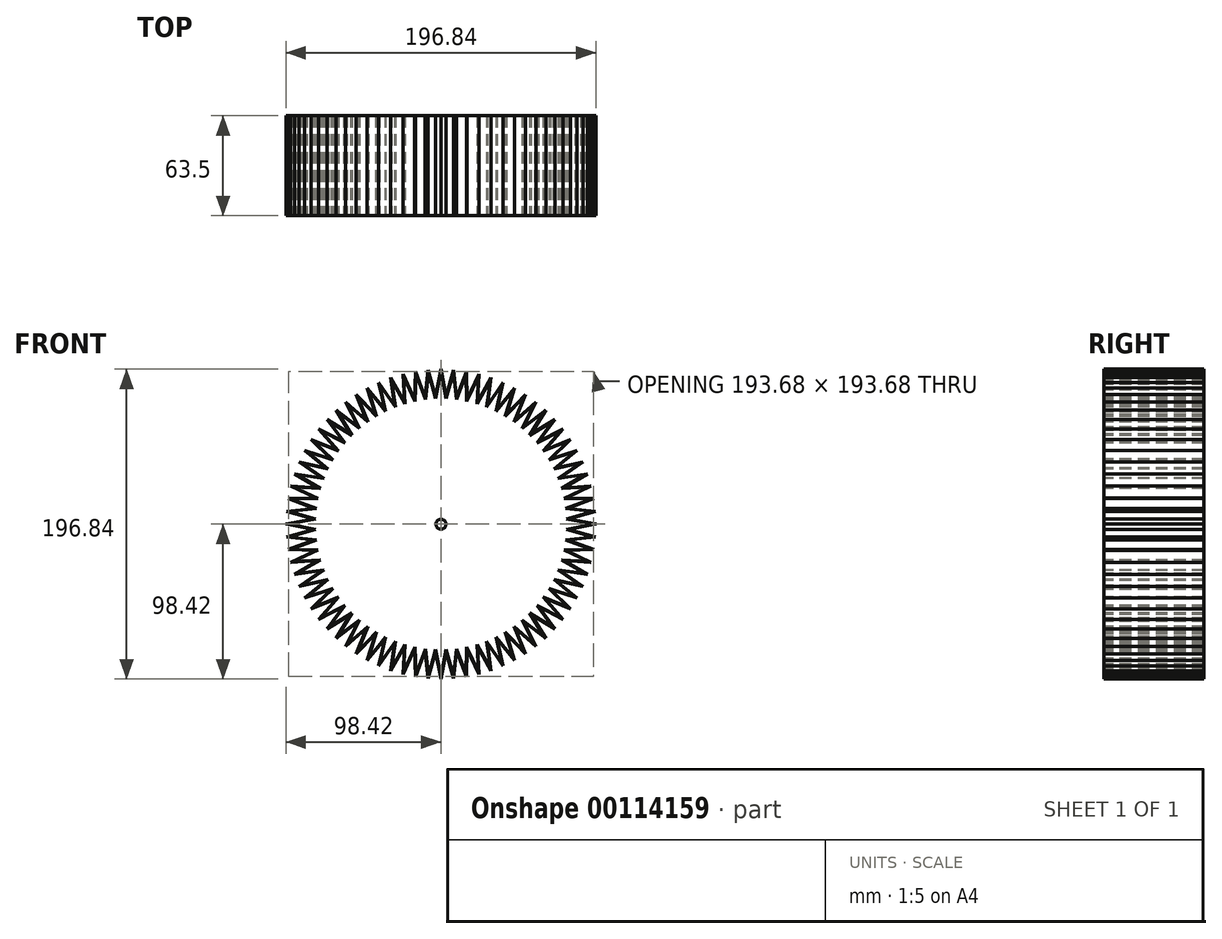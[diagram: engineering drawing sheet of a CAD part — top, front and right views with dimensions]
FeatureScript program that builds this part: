
annotation { "Feature Type Name" : "Feature", "Feature Type Description" : "" }
export const myFeature = defineFeature(function(context is Context, id is Id, definition is map)
    precondition{}
    {
        {
            var Q0;
            Q0=qCreatedBy(makeId("Front.planeOp"),FACE);
            var sketch = newSketch(context, id + "F0", { "sketchPlane" : qUnion([Q0])});
            skCircle(sketch, "E0", {"center": v(0, 0) * mm, "radius": 98.43 * mm});
            skCircle(sketch, "E1", {"center": v(0, 0) * mm, "radius": 79.38 * mm});
            skPoint(sketch, "E2", {"position": v(0, 98.43) * mm});
            skPoint(sketch, "E3", {"position": v(0, 96.84) * mm});
            skPoint(sketch, "E4", {"position": v(-3.37, 80.9) * mm});
            skPoint(sketch, "E5", {"position": v(3.37, 80.9) * mm});
            skLineSegment(sketch, "E6", {"start": v(0, 96.84) * mm, "end": v(-3.37, 79.3) * mm});
            skLineSegment(sketch, "E7", {"start": v(0, 96.84) * mm, "end": v(3.37, 79.3) * mm});
            skLineSegment(sketch, "E8", {"start": v(3.37, 80.9) * mm, "end": v(0, 98.43) * mm});
            skLineSegment(sketch, "E9", {"start": v(0, 98.43) * mm, "end": v(-3.37, 80.9) * mm});
            skLineSegment(sketch, "E10.1.0", {"start": v(-8, 96.5) * mm, "end": v(-9.9, 78.75) * mm});
            skPoint(sketch, "E10.1.1", {"position": v(-8.13, 98.09) * mm});
            skPoint(sketch, "E10.1.2", {"position": v(-8, 96.5) * mm});
            skPoint(sketch, "E10.1.3", {"position": v(-10.04, 80.34) * mm});
            skLineSegment(sketch, "E10.1.4", {"start": v(-8.13, 98.09) * mm, "end": v(-10.04, 80.34) * mm});
            skPoint(sketch, "E10.1.5", {"position": v(-3.32, 80.9) * mm});
            skLineSegment(sketch, "E10.1.6", {"start": v(-8, 96.5) * mm, "end": v(-3.19, 79.31) * mm});
            skLineSegment(sketch, "E10.1.7", {"start": v(-3.32, 80.9) * mm, "end": v(-8.13, 98.09) * mm});
            skLineSegment(sketch, "E10.2.0", {"start": v(-15.94, 95.52) * mm, "end": v(-16.38, 77.67) * mm});
            skPoint(sketch, "E10.2.1", {"position": v(-16.2, 97.08) * mm});
            skPoint(sketch, "E10.2.2", {"position": v(-15.94, 95.52) * mm});
            skPoint(sketch, "E10.2.3", {"position": v(-16.64, 79.23) * mm});
            skLineSegment(sketch, "E10.2.4", {"start": v(-16.2, 97.08) * mm, "end": v(-16.64, 79.23) * mm});
            skPoint(sketch, "E10.2.5", {"position": v(-9.99, 80.34) * mm});
            skLineSegment(sketch, "E10.2.6", {"start": v(-15.94, 95.52) * mm, "end": v(-9.73, 78.78) * mm});
            skLineSegment(sketch, "E10.2.7", {"start": v(-9.99, 80.34) * mm, "end": v(-16.2, 97.08) * mm});
            skLineSegment(sketch, "E10.3.0", {"start": v(-23.77, 93.87) * mm, "end": v(-22.74, 76.05) * mm});
            skPoint(sketch, "E10.3.1", {"position": v(-24.16, 95.41) * mm});
            skPoint(sketch, "E10.3.2", {"position": v(-23.77, 93.87) * mm});
            skPoint(sketch, "E10.3.3", {"position": v(-23.13, 77.59) * mm});
            skLineSegment(sketch, "E10.3.4", {"start": v(-24.16, 95.41) * mm, "end": v(-23.13, 77.59) * mm});
            skPoint(sketch, "E10.3.5", {"position": v(-16.59, 79.24) * mm});
            skLineSegment(sketch, "E10.3.6", {"start": v(-23.77, 93.87) * mm, "end": v(-16.2, 77.7) * mm});
            skLineSegment(sketch, "E10.3.7", {"start": v(-16.59, 79.24) * mm, "end": v(-24.16, 95.41) * mm});
            skLineSegment(sketch, "E10.4.0", {"start": v(-31.44, 91.6) * mm, "end": v(-28.94, 73.91) * mm});
            skPoint(sketch, "E10.4.1", {"position": v(-31.96, 93.1) * mm});
            skPoint(sketch, "E10.4.2", {"position": v(-31.44, 91.6) * mm});
            skPoint(sketch, "E10.4.3", {"position": v(-29.45, 75.41) * mm});
            skLineSegment(sketch, "E10.4.4", {"start": v(-31.96, 93.1) * mm, "end": v(-29.45, 75.41) * mm});
            skPoint(sketch, "E10.4.5", {"position": v(-23.08, 77.6) * mm});
            skLineSegment(sketch, "E10.4.6", {"start": v(-31.44, 91.6) * mm, "end": v(-22.56, 76.1) * mm});
            skLineSegment(sketch, "E10.4.7", {"start": v(-23.08, 77.6) * mm, "end": v(-31.96, 93.1) * mm});
            skLineSegment(sketch, "E10.5.0", {"start": v(-38.9, 88.68) * mm, "end": v(-34.94, 71.27) * mm});
            skPoint(sketch, "E10.5.1", {"position": v(-39.54, 90.13) * mm});
            skPoint(sketch, "E10.5.2", {"position": v(-38.9, 88.68) * mm});
            skPoint(sketch, "E10.5.3", {"position": v(-35.58, 72.72) * mm});
            skLineSegment(sketch, "E10.5.4", {"start": v(-39.54, 90.13) * mm, "end": v(-35.58, 72.72) * mm});
            skPoint(sketch, "E10.5.5", {"position": v(-29.4, 75.43) * mm});
            skLineSegment(sketch, "E10.5.6", {"start": v(-38.9, 88.68) * mm, "end": v(-28.77, 73.98) * mm});
            skLineSegment(sketch, "E10.5.7", {"start": v(-29.4, 75.43) * mm, "end": v(-39.54, 90.13) * mm});
            skLineSegment(sketch, "E10.6.0", {"start": v(-46.09, 85.17) * mm, "end": v(-40.7, 68.14) * mm});
            skPoint(sketch, "E10.6.1", {"position": v(-46.85, 86.56) * mm});
            skPoint(sketch, "E10.6.2", {"position": v(-46.09, 85.17) * mm});
            skPoint(sketch, "E10.6.3", {"position": v(-41.47, 69.54) * mm});
            skLineSegment(sketch, "E10.6.4", {"start": v(-46.85, 86.56) * mm, "end": v(-41.47, 69.54) * mm});
            skPoint(sketch, "E10.6.5", {"position": v(-35.53, 72.75) * mm});
            skLineSegment(sketch, "E10.6.6", {"start": v(-46.09, 85.17) * mm, "end": v(-34.78, 71.35) * mm});
            skLineSegment(sketch, "E10.6.7", {"start": v(-35.53, 72.75) * mm, "end": v(-46.85, 86.56) * mm});
            skLineSegment(sketch, "E10.7.0", {"start": v(-52.97, 81.07) * mm, "end": v(-46.2, 64.55) * mm});
            skPoint(sketch, "E10.7.1", {"position": v(-53.83, 82.4) * mm});
            skPoint(sketch, "E10.7.2", {"position": v(-52.97, 81.07) * mm});
            skPoint(sketch, "E10.7.3", {"position": v(-47.07, 65.87) * mm});
            skLineSegment(sketch, "E10.7.4", {"start": v(-53.83, 82.4) * mm, "end": v(-47.07, 65.87) * mm});
            skPoint(sketch, "E10.7.5", {"position": v(-41.42, 69.56) * mm});
            skLineSegment(sketch, "E10.7.6", {"start": v(-52.97, 81.07) * mm, "end": v(-40.55, 68.23) * mm});
            skLineSegment(sketch, "E10.7.7", {"start": v(-41.42, 69.56) * mm, "end": v(-53.83, 82.4) * mm});
            skLineSegment(sketch, "E10.8.0", {"start": v(-59.48, 76.42) * mm, "end": v(-51.37, 60.51) * mm});
            skPoint(sketch, "E10.8.1", {"position": v(-60.45, 77.67) * mm});
            skPoint(sketch, "E10.8.2", {"position": v(-59.48, 76.42) * mm});
            skPoint(sketch, "E10.8.3", {"position": v(-52.34, 61.76) * mm});
            skLineSegment(sketch, "E10.8.4", {"start": v(-60.45, 77.67) * mm, "end": v(-52.34, 61.76) * mm});
            skPoint(sketch, "E10.8.5", {"position": v(-47.02, 65.9) * mm});
            skLineSegment(sketch, "E10.8.6", {"start": v(-59.48, 76.42) * mm, "end": v(-46.05, 64.65) * mm});
            skLineSegment(sketch, "E10.8.7", {"start": v(-47.02, 65.9) * mm, "end": v(-60.45, 77.67) * mm});
            skLineSegment(sketch, "E10.9.0", {"start": v(-65.59, 71.25) * mm, "end": v(-56.2, 56.06) * mm});
            skPoint(sketch, "E10.9.1", {"position": v(-66.66, 72.41) * mm});
            skPoint(sketch, "E10.9.2", {"position": v(-65.59, 71.25) * mm});
            skPoint(sketch, "E10.9.3", {"position": v(-57.27, 57.23) * mm});
            skLineSegment(sketch, "E10.9.4", {"start": v(-66.66, 72.41) * mm, "end": v(-57.27, 57.23) * mm});
            skPoint(sketch, "E10.9.5", {"position": v(-52.3, 61.8) * mm});
            skLineSegment(sketch, "E10.9.6", {"start": v(-65.59, 71.25) * mm, "end": v(-51.23, 60.63) * mm});
            skLineSegment(sketch, "E10.9.7", {"start": v(-52.3, 61.8) * mm, "end": v(-66.66, 72.41) * mm});
            skLineSegment(sketch, "E10.10.0", {"start": v(-71.25, 65.59) * mm, "end": v(-60.63, 51.23) * mm});
            skPoint(sketch, "E10.10.1", {"position": v(-72.41, 66.66) * mm});
            skPoint(sketch, "E10.10.2", {"position": v(-71.25, 65.59) * mm});
            skPoint(sketch, "E10.10.3", {"position": v(-61.8, 52.3) * mm});
            skLineSegment(sketch, "E10.10.4", {"start": v(-72.41, 66.66) * mm, "end": v(-61.8, 52.3) * mm});
            skPoint(sketch, "E10.10.5", {"position": v(-57.23, 57.27) * mm});
            skLineSegment(sketch, "E10.10.6", {"start": v(-71.25, 65.59) * mm, "end": v(-56.06, 56.2) * mm});
            skLineSegment(sketch, "E10.10.7", {"start": v(-57.23, 57.27) * mm, "end": v(-72.41, 66.66) * mm});
            skLineSegment(sketch, "E10.11.0", {"start": v(-76.42, 59.48) * mm, "end": v(-64.65, 46.05) * mm});
            skPoint(sketch, "E10.11.1", {"position": v(-77.67, 60.45) * mm});
            skPoint(sketch, "E10.11.2", {"position": v(-76.42, 59.48) * mm});
            skPoint(sketch, "E10.11.3", {"position": v(-65.9, 47.02) * mm});
            skLineSegment(sketch, "E10.11.4", {"start": v(-77.67, 60.45) * mm, "end": v(-65.9, 47.02) * mm});
            skPoint(sketch, "E10.11.5", {"position": v(-61.76, 52.34) * mm});
            skLineSegment(sketch, "E10.11.6", {"start": v(-76.42, 59.48) * mm, "end": v(-60.51, 51.37) * mm});
            skLineSegment(sketch, "E10.11.7", {"start": v(-61.76, 52.34) * mm, "end": v(-77.67, 60.45) * mm});
            skLineSegment(sketch, "E10.12.0", {"start": v(-81.07, 52.97) * mm, "end": v(-68.23, 40.55) * mm});
            skPoint(sketch, "E10.12.1", {"position": v(-82.4, 53.83) * mm});
            skPoint(sketch, "E10.12.2", {"position": v(-81.07, 52.97) * mm});
            skPoint(sketch, "E10.12.3", {"position": v(-69.56, 41.42) * mm});
            skLineSegment(sketch, "E10.12.4", {"start": v(-82.4, 53.83) * mm, "end": v(-69.56, 41.42) * mm});
            skPoint(sketch, "E10.12.5", {"position": v(-65.87, 47.07) * mm});
            skLineSegment(sketch, "E10.12.6", {"start": v(-81.07, 52.97) * mm, "end": v(-64.55, 46.2) * mm});
            skLineSegment(sketch, "E10.12.7", {"start": v(-65.87, 47.07) * mm, "end": v(-82.4, 53.83) * mm});
            skLineSegment(sketch, "E10.13.0", {"start": v(-85.17, 46.09) * mm, "end": v(-71.35, 34.78) * mm});
            skPoint(sketch, "E10.13.1", {"position": v(-86.56, 46.85) * mm});
            skPoint(sketch, "E10.13.2", {"position": v(-85.17, 46.09) * mm});
            skPoint(sketch, "E10.13.3", {"position": v(-72.75, 35.53) * mm});
            skLineSegment(sketch, "E10.13.4", {"start": v(-86.56, 46.85) * mm, "end": v(-72.75, 35.53) * mm});
            skPoint(sketch, "E10.13.5", {"position": v(-69.54, 41.47) * mm});
            skLineSegment(sketch, "E10.13.6", {"start": v(-85.17, 46.09) * mm, "end": v(-68.14, 40.7) * mm});
            skLineSegment(sketch, "E10.13.7", {"start": v(-69.54, 41.47) * mm, "end": v(-86.56, 46.85) * mm});
            skLineSegment(sketch, "E10.14.0", {"start": v(-88.68, 38.9) * mm, "end": v(-73.98, 28.77) * mm});
            skPoint(sketch, "E10.14.1", {"position": v(-90.13, 39.54) * mm});
            skPoint(sketch, "E10.14.2", {"position": v(-88.68, 38.9) * mm});
            skPoint(sketch, "E10.14.3", {"position": v(-75.43, 29.4) * mm});
            skLineSegment(sketch, "E10.14.4", {"start": v(-90.13, 39.54) * mm, "end": v(-75.43, 29.4) * mm});
            skPoint(sketch, "E10.14.5", {"position": v(-72.72, 35.58) * mm});
            skLineSegment(sketch, "E10.14.6", {"start": v(-88.68, 38.9) * mm, "end": v(-71.27, 34.94) * mm});
            skLineSegment(sketch, "E10.14.7", {"start": v(-72.72, 35.58) * mm, "end": v(-90.13, 39.54) * mm});
            skLineSegment(sketch, "E10.15.0", {"start": v(-91.6, 31.44) * mm, "end": v(-76.1, 22.56) * mm});
            skPoint(sketch, "E10.15.1", {"position": v(-93.1, 31.96) * mm});
            skPoint(sketch, "E10.15.2", {"position": v(-91.6, 31.44) * mm});
            skPoint(sketch, "E10.15.3", {"position": v(-77.6, 23.08) * mm});
            skLineSegment(sketch, "E10.15.4", {"start": v(-93.1, 31.96) * mm, "end": v(-77.6, 23.08) * mm});
            skPoint(sketch, "E10.15.5", {"position": v(-75.41, 29.45) * mm});
            skLineSegment(sketch, "E10.15.6", {"start": v(-91.6, 31.44) * mm, "end": v(-73.91, 28.94) * mm});
            skLineSegment(sketch, "E10.15.7", {"start": v(-75.41, 29.45) * mm, "end": v(-93.1, 31.96) * mm});
            skLineSegment(sketch, "E10.16.0", {"start": v(-93.87, 23.77) * mm, "end": v(-77.7, 16.2) * mm});
            skPoint(sketch, "E10.16.1", {"position": v(-95.41, 24.16) * mm});
            skPoint(sketch, "E10.16.2", {"position": v(-93.87, 23.77) * mm});
            skPoint(sketch, "E10.16.3", {"position": v(-79.24, 16.59) * mm});
            skLineSegment(sketch, "E10.16.4", {"start": v(-95.41, 24.16) * mm, "end": v(-79.24, 16.59) * mm});
            skPoint(sketch, "E10.16.5", {"position": v(-77.59, 23.13) * mm});
            skLineSegment(sketch, "E10.16.6", {"start": v(-93.87, 23.77) * mm, "end": v(-76.05, 22.74) * mm});
            skLineSegment(sketch, "E10.16.7", {"start": v(-77.59, 23.13) * mm, "end": v(-95.41, 24.16) * mm});
            skLineSegment(sketch, "E10.17.0", {"start": v(-95.52, 15.94) * mm, "end": v(-78.78, 9.73) * mm});
            skPoint(sketch, "E10.17.1", {"position": v(-97.08, 16.2) * mm});
            skPoint(sketch, "E10.17.2", {"position": v(-95.52, 15.94) * mm});
            skPoint(sketch, "E10.17.3", {"position": v(-80.34, 9.99) * mm});
            skLineSegment(sketch, "E10.17.4", {"start": v(-97.08, 16.2) * mm, "end": v(-80.34, 9.99) * mm});
            skPoint(sketch, "E10.17.5", {"position": v(-79.23, 16.64) * mm});
            skLineSegment(sketch, "E10.17.6", {"start": v(-95.52, 15.94) * mm, "end": v(-77.67, 16.38) * mm});
            skLineSegment(sketch, "E10.17.7", {"start": v(-79.23, 16.64) * mm, "end": v(-97.08, 16.2) * mm});
            skLineSegment(sketch, "E10.18.0", {"start": v(-96.5, 8) * mm, "end": v(-79.31, 3.19) * mm});
            skPoint(sketch, "E10.18.1", {"position": v(-98.09, 8.13) * mm});
            skPoint(sketch, "E10.18.2", {"position": v(-96.5, 8) * mm});
            skPoint(sketch, "E10.18.3", {"position": v(-80.9, 3.32) * mm});
            skLineSegment(sketch, "E10.18.4", {"start": v(-98.09, 8.13) * mm, "end": v(-80.9, 3.32) * mm});
            skPoint(sketch, "E10.18.5", {"position": v(-80.34, 10.04) * mm});
            skLineSegment(sketch, "E10.18.6", {"start": v(-96.5, 8) * mm, "end": v(-78.75, 9.9) * mm});
            skLineSegment(sketch, "E10.18.7", {"start": v(-80.34, 10.04) * mm, "end": v(-98.09, 8.13) * mm});
            skLineSegment(sketch, "E10.19.0", {"start": v(-96.84, 0) * mm, "end": v(-79.3, -3.37) * mm});
            skPoint(sketch, "E10.19.1", {"position": v(-98.43, 0) * mm});
            skPoint(sketch, "E10.19.2", {"position": v(-96.84, 0) * mm});
            skPoint(sketch, "E10.19.3", {"position": v(-80.9, -3.37) * mm});
            skLineSegment(sketch, "E10.19.4", {"start": v(-98.43, 0) * mm, "end": v(-80.9, -3.37) * mm});
            skPoint(sketch, "E10.19.5", {"position": v(-80.9, 3.37) * mm});
            skLineSegment(sketch, "E10.19.6", {"start": v(-96.84, 0) * mm, "end": v(-79.3, 3.37) * mm});
            skLineSegment(sketch, "E10.19.7", {"start": v(-80.9, 3.37) * mm, "end": v(-98.42, 0) * mm});
            skLineSegment(sketch, "E10.20.0", {"start": v(-96.5, -8) * mm, "end": v(-78.75, -9.9) * mm});
            skPoint(sketch, "E10.20.1", {"position": v(-98.09, -8.13) * mm});
            skPoint(sketch, "E10.20.2", {"position": v(-96.5, -8) * mm});
            skPoint(sketch, "E10.20.3", {"position": v(-80.34, -10.04) * mm});
            skLineSegment(sketch, "E10.20.4", {"start": v(-98.09, -8.13) * mm, "end": v(-80.34, -10.04) * mm});
            skPoint(sketch, "E10.20.5", {"position": v(-80.9, -3.32) * mm});
            skLineSegment(sketch, "E10.20.6", {"start": v(-96.5, -8) * mm, "end": v(-79.31, -3.19) * mm});
            skLineSegment(sketch, "E10.20.7", {"start": v(-80.9, -3.32) * mm, "end": v(-98.09, -8.13) * mm});
            skLineSegment(sketch, "E10.21.0", {"start": v(-95.52, -15.94) * mm, "end": v(-77.67, -16.38) * mm});
            skPoint(sketch, "E10.21.1", {"position": v(-97.08, -16.2) * mm});
            skPoint(sketch, "E10.21.2", {"position": v(-95.52, -15.94) * mm});
            skPoint(sketch, "E10.21.3", {"position": v(-79.23, -16.64) * mm});
            skLineSegment(sketch, "E10.21.4", {"start": v(-97.08, -16.2) * mm, "end": v(-79.23, -16.64) * mm});
            skPoint(sketch, "E10.21.5", {"position": v(-80.34, -9.99) * mm});
            skLineSegment(sketch, "E10.21.6", {"start": v(-95.52, -15.94) * mm, "end": v(-78.78, -9.73) * mm});
            skLineSegment(sketch, "E10.21.7", {"start": v(-80.34, -9.99) * mm, "end": v(-97.08, -16.2) * mm});
            skLineSegment(sketch, "E10.22.0", {"start": v(-93.87, -23.77) * mm, "end": v(-76.05, -22.74) * mm});
            skPoint(sketch, "E10.22.1", {"position": v(-95.41, -24.16) * mm});
            skPoint(sketch, "E10.22.2", {"position": v(-93.87, -23.77) * mm});
            skPoint(sketch, "E10.22.3", {"position": v(-77.59, -23.13) * mm});
            skLineSegment(sketch, "E10.22.4", {"start": v(-95.41, -24.16) * mm, "end": v(-77.59, -23.13) * mm});
            skPoint(sketch, "E10.22.5", {"position": v(-79.24, -16.59) * mm});
            skLineSegment(sketch, "E10.22.6", {"start": v(-93.87, -23.77) * mm, "end": v(-77.7, -16.2) * mm});
            skLineSegment(sketch, "E10.22.7", {"start": v(-79.24, -16.59) * mm, "end": v(-95.41, -24.16) * mm});
            skLineSegment(sketch, "E10.23.0", {"start": v(-91.6, -31.44) * mm, "end": v(-73.91, -28.94) * mm});
            skPoint(sketch, "E10.23.1", {"position": v(-93.1, -31.96) * mm});
            skPoint(sketch, "E10.23.2", {"position": v(-91.6, -31.44) * mm});
            skPoint(sketch, "E10.23.3", {"position": v(-75.41, -29.45) * mm});
            skLineSegment(sketch, "E10.23.4", {"start": v(-93.1, -31.96) * mm, "end": v(-75.41, -29.45) * mm});
            skPoint(sketch, "E10.23.5", {"position": v(-77.6, -23.08) * mm});
            skLineSegment(sketch, "E10.23.6", {"start": v(-91.6, -31.44) * mm, "end": v(-76.1, -22.56) * mm});
            skLineSegment(sketch, "E10.23.7", {"start": v(-77.6, -23.08) * mm, "end": v(-93.1, -31.96) * mm});
            skLineSegment(sketch, "E10.24.0", {"start": v(-88.68, -38.9) * mm, "end": v(-71.27, -34.94) * mm});
            skPoint(sketch, "E10.24.1", {"position": v(-90.13, -39.54) * mm});
            skPoint(sketch, "E10.24.2", {"position": v(-88.68, -38.9) * mm});
            skPoint(sketch, "E10.24.3", {"position": v(-72.72, -35.58) * mm});
            skLineSegment(sketch, "E10.24.4", {"start": v(-90.13, -39.54) * mm, "end": v(-72.72, -35.58) * mm});
            skPoint(sketch, "E10.24.5", {"position": v(-75.43, -29.4) * mm});
            skLineSegment(sketch, "E10.24.6", {"start": v(-88.68, -38.9) * mm, "end": v(-73.98, -28.77) * mm});
            skLineSegment(sketch, "E10.24.7", {"start": v(-75.43, -29.4) * mm, "end": v(-90.13, -39.54) * mm});
            skLineSegment(sketch, "E10.25.0", {"start": v(-85.17, -46.09) * mm, "end": v(-68.14, -40.7) * mm});
            skPoint(sketch, "E10.25.1", {"position": v(-86.56, -46.85) * mm});
            skPoint(sketch, "E10.25.2", {"position": v(-85.17, -46.09) * mm});
            skPoint(sketch, "E10.25.3", {"position": v(-69.54, -41.47) * mm});
            skLineSegment(sketch, "E10.25.4", {"start": v(-86.56, -46.85) * mm, "end": v(-69.54, -41.47) * mm});
            skPoint(sketch, "E10.25.5", {"position": v(-72.75, -35.53) * mm});
            skLineSegment(sketch, "E10.25.6", {"start": v(-85.17, -46.09) * mm, "end": v(-71.35, -34.78) * mm});
            skLineSegment(sketch, "E10.25.7", {"start": v(-72.75, -35.53) * mm, "end": v(-86.56, -46.85) * mm});
            skLineSegment(sketch, "E10.26.0", {"start": v(-81.07, -52.97) * mm, "end": v(-64.55, -46.2) * mm});
            skPoint(sketch, "E10.26.1", {"position": v(-82.4, -53.83) * mm});
            skPoint(sketch, "E10.26.2", {"position": v(-81.07, -52.97) * mm});
            skPoint(sketch, "E10.26.3", {"position": v(-65.87, -47.07) * mm});
            skLineSegment(sketch, "E10.26.4", {"start": v(-82.4, -53.83) * mm, "end": v(-65.87, -47.07) * mm});
            skPoint(sketch, "E10.26.5", {"position": v(-69.56, -41.42) * mm});
            skLineSegment(sketch, "E10.26.6", {"start": v(-81.07, -52.97) * mm, "end": v(-68.23, -40.55) * mm});
            skLineSegment(sketch, "E10.26.7", {"start": v(-69.56, -41.42) * mm, "end": v(-82.4, -53.83) * mm});
            skLineSegment(sketch, "E10.27.0", {"start": v(-76.42, -59.48) * mm, "end": v(-60.51, -51.37) * mm});
            skPoint(sketch, "E10.27.1", {"position": v(-77.67, -60.45) * mm});
            skPoint(sketch, "E10.27.2", {"position": v(-76.42, -59.48) * mm});
            skPoint(sketch, "E10.27.3", {"position": v(-61.76, -52.34) * mm});
            skLineSegment(sketch, "E10.27.4", {"start": v(-77.67, -60.45) * mm, "end": v(-61.76, -52.34) * mm});
            skPoint(sketch, "E10.27.5", {"position": v(-65.9, -47.02) * mm});
            skLineSegment(sketch, "E10.27.6", {"start": v(-76.42, -59.48) * mm, "end": v(-64.65, -46.05) * mm});
            skLineSegment(sketch, "E10.27.7", {"start": v(-65.9, -47.02) * mm, "end": v(-77.67, -60.45) * mm});
            skLineSegment(sketch, "E10.28.0", {"start": v(-71.25, -65.59) * mm, "end": v(-56.06, -56.2) * mm});
            skPoint(sketch, "E10.28.1", {"position": v(-72.41, -66.66) * mm});
            skPoint(sketch, "E10.28.2", {"position": v(-71.25, -65.59) * mm});
            skPoint(sketch, "E10.28.3", {"position": v(-57.23, -57.27) * mm});
            skLineSegment(sketch, "E10.28.4", {"start": v(-72.41, -66.66) * mm, "end": v(-57.23, -57.27) * mm});
            skPoint(sketch, "E10.28.5", {"position": v(-61.8, -52.3) * mm});
            skLineSegment(sketch, "E10.28.6", {"start": v(-71.25, -65.59) * mm, "end": v(-60.63, -51.23) * mm});
            skLineSegment(sketch, "E10.28.7", {"start": v(-61.8, -52.3) * mm, "end": v(-72.41, -66.66) * mm});
            skLineSegment(sketch, "E10.29.0", {"start": v(-65.59, -71.25) * mm, "end": v(-51.23, -60.63) * mm});
            skPoint(sketch, "E10.29.1", {"position": v(-66.66, -72.41) * mm});
            skPoint(sketch, "E10.29.2", {"position": v(-65.59, -71.25) * mm});
            skPoint(sketch, "E10.29.3", {"position": v(-52.3, -61.8) * mm});
            skLineSegment(sketch, "E10.29.4", {"start": v(-66.66, -72.41) * mm, "end": v(-52.3, -61.8) * mm});
            skPoint(sketch, "E10.29.5", {"position": v(-57.27, -57.23) * mm});
            skLineSegment(sketch, "E10.29.6", {"start": v(-65.59, -71.25) * mm, "end": v(-56.2, -56.06) * mm});
            skLineSegment(sketch, "E10.29.7", {"start": v(-57.27, -57.23) * mm, "end": v(-66.66, -72.41) * mm});
            skLineSegment(sketch, "E10.30.0", {"start": v(-59.48, -76.42) * mm, "end": v(-46.05, -64.65) * mm});
            skPoint(sketch, "E10.30.1", {"position": v(-60.45, -77.67) * mm});
            skPoint(sketch, "E10.30.2", {"position": v(-59.48, -76.42) * mm});
            skPoint(sketch, "E10.30.3", {"position": v(-47.02, -65.9) * mm});
            skLineSegment(sketch, "E10.30.4", {"start": v(-60.45, -77.67) * mm, "end": v(-47.02, -65.9) * mm});
            skPoint(sketch, "E10.30.5", {"position": v(-52.34, -61.76) * mm});
            skLineSegment(sketch, "E10.30.6", {"start": v(-59.48, -76.42) * mm, "end": v(-51.37, -60.51) * mm});
            skLineSegment(sketch, "E10.30.7", {"start": v(-52.34, -61.76) * mm, "end": v(-60.45, -77.67) * mm});
            skLineSegment(sketch, "E10.31.0", {"start": v(-52.97, -81.07) * mm, "end": v(-40.55, -68.23) * mm});
            skPoint(sketch, "E10.31.1", {"position": v(-53.83, -82.4) * mm});
            skPoint(sketch, "E10.31.2", {"position": v(-52.97, -81.07) * mm});
            skPoint(sketch, "E10.31.3", {"position": v(-41.42, -69.56) * mm});
            skLineSegment(sketch, "E10.31.4", {"start": v(-53.83, -82.4) * mm, "end": v(-41.42, -69.56) * mm});
            skPoint(sketch, "E10.31.5", {"position": v(-47.07, -65.87) * mm});
            skLineSegment(sketch, "E10.31.6", {"start": v(-52.97, -81.07) * mm, "end": v(-46.2, -64.55) * mm});
            skLineSegment(sketch, "E10.31.7", {"start": v(-47.07, -65.87) * mm, "end": v(-53.83, -82.4) * mm});
            skLineSegment(sketch, "E10.32.0", {"start": v(-46.09, -85.17) * mm, "end": v(-34.78, -71.35) * mm});
            skPoint(sketch, "E10.32.1", {"position": v(-46.85, -86.56) * mm});
            skPoint(sketch, "E10.32.2", {"position": v(-46.09, -85.17) * mm});
            skPoint(sketch, "E10.32.3", {"position": v(-35.53, -72.75) * mm});
            skLineSegment(sketch, "E10.32.4", {"start": v(-46.85, -86.56) * mm, "end": v(-35.53, -72.75) * mm});
            skPoint(sketch, "E10.32.5", {"position": v(-41.47, -69.54) * mm});
            skLineSegment(sketch, "E10.32.6", {"start": v(-46.09, -85.17) * mm, "end": v(-40.7, -68.14) * mm});
            skLineSegment(sketch, "E10.32.7", {"start": v(-41.47, -69.54) * mm, "end": v(-46.85, -86.56) * mm});
            skLineSegment(sketch, "E10.33.0", {"start": v(-38.9, -88.68) * mm, "end": v(-28.77, -73.98) * mm});
            skPoint(sketch, "E10.33.1", {"position": v(-39.54, -90.13) * mm});
            skPoint(sketch, "E10.33.2", {"position": v(-38.9, -88.68) * mm});
            skPoint(sketch, "E10.33.3", {"position": v(-29.4, -75.43) * mm});
            skLineSegment(sketch, "E10.33.4", {"start": v(-39.54, -90.13) * mm, "end": v(-29.4, -75.43) * mm});
            skPoint(sketch, "E10.33.5", {"position": v(-35.58, -72.72) * mm});
            skLineSegment(sketch, "E10.33.6", {"start": v(-38.9, -88.68) * mm, "end": v(-34.94, -71.27) * mm});
            skLineSegment(sketch, "E10.33.7", {"start": v(-35.58, -72.72) * mm, "end": v(-39.54, -90.13) * mm});
            skLineSegment(sketch, "E10.34.0", {"start": v(-31.44, -91.6) * mm, "end": v(-22.56, -76.1) * mm});
            skPoint(sketch, "E10.34.1", {"position": v(-31.96, -93.1) * mm});
            skPoint(sketch, "E10.34.2", {"position": v(-31.44, -91.6) * mm});
            skPoint(sketch, "E10.34.3", {"position": v(-23.08, -77.6) * mm});
            skLineSegment(sketch, "E10.34.4", {"start": v(-31.96, -93.1) * mm, "end": v(-23.08, -77.6) * mm});
            skPoint(sketch, "E10.34.5", {"position": v(-29.45, -75.41) * mm});
            skLineSegment(sketch, "E10.34.6", {"start": v(-31.44, -91.6) * mm, "end": v(-28.94, -73.91) * mm});
            skLineSegment(sketch, "E10.34.7", {"start": v(-29.45, -75.41) * mm, "end": v(-31.96, -93.1) * mm});
            skLineSegment(sketch, "E10.35.0", {"start": v(-23.77, -93.87) * mm, "end": v(-16.2, -77.7) * mm});
            skPoint(sketch, "E10.35.1", {"position": v(-24.16, -95.41) * mm});
            skPoint(sketch, "E10.35.2", {"position": v(-23.77, -93.87) * mm});
            skPoint(sketch, "E10.35.3", {"position": v(-16.59, -79.24) * mm});
            skLineSegment(sketch, "E10.35.4", {"start": v(-24.16, -95.41) * mm, "end": v(-16.59, -79.24) * mm});
            skPoint(sketch, "E10.35.5", {"position": v(-23.13, -77.59) * mm});
            skLineSegment(sketch, "E10.35.6", {"start": v(-23.77, -93.87) * mm, "end": v(-22.74, -76.05) * mm});
            skLineSegment(sketch, "E10.35.7", {"start": v(-23.13, -77.59) * mm, "end": v(-24.16, -95.41) * mm});
            skLineSegment(sketch, "E10.36.0", {"start": v(-15.94, -95.52) * mm, "end": v(-9.73, -78.78) * mm});
            skPoint(sketch, "E10.36.1", {"position": v(-16.2, -97.08) * mm});
            skPoint(sketch, "E10.36.2", {"position": v(-15.94, -95.52) * mm});
            skPoint(sketch, "E10.36.3", {"position": v(-9.99, -80.34) * mm});
            skLineSegment(sketch, "E10.36.4", {"start": v(-16.2, -97.08) * mm, "end": v(-9.99, -80.34) * mm});
            skPoint(sketch, "E10.36.5", {"position": v(-16.64, -79.23) * mm});
            skLineSegment(sketch, "E10.36.6", {"start": v(-15.94, -95.52) * mm, "end": v(-16.38, -77.67) * mm});
            skLineSegment(sketch, "E10.36.7", {"start": v(-16.64, -79.23) * mm, "end": v(-16.2, -97.08) * mm});
            skLineSegment(sketch, "E10.37.0", {"start": v(-8, -96.5) * mm, "end": v(-3.19, -79.31) * mm});
            skPoint(sketch, "E10.37.1", {"position": v(-8.13, -98.09) * mm});
            skPoint(sketch, "E10.37.2", {"position": v(-8, -96.5) * mm});
            skPoint(sketch, "E10.37.3", {"position": v(-3.32, -80.9) * mm});
            skLineSegment(sketch, "E10.37.4", {"start": v(-8.13, -98.09) * mm, "end": v(-3.32, -80.9) * mm});
            skPoint(sketch, "E10.37.5", {"position": v(-10.04, -80.34) * mm});
            skLineSegment(sketch, "E10.37.6", {"start": v(-8, -96.5) * mm, "end": v(-9.9, -78.75) * mm});
            skLineSegment(sketch, "E10.37.7", {"start": v(-10.04, -80.34) * mm, "end": v(-8.13, -98.09) * mm});
            skLineSegment(sketch, "E10.38.0", {"start": v(0, -96.84) * mm, "end": v(3.37, -79.3) * mm});
            skPoint(sketch, "E10.38.1", {"position": v(0, -98.43) * mm});
            skPoint(sketch, "E10.38.2", {"position": v(0, -96.84) * mm});
            skPoint(sketch, "E10.38.3", {"position": v(3.37, -80.9) * mm});
            skLineSegment(sketch, "E10.38.4", {"start": v(0, -98.43) * mm, "end": v(3.37, -80.9) * mm});
            skPoint(sketch, "E10.38.5", {"position": v(-3.37, -80.9) * mm});
            skLineSegment(sketch, "E10.38.6", {"start": v(0, -96.84) * mm, "end": v(-3.37, -79.3) * mm});
            skLineSegment(sketch, "E10.38.7", {"start": v(-3.37, -80.9) * mm, "end": v(0, -98.43) * mm});
            skLineSegment(sketch, "E10.39.0", {"start": v(8, -96.5) * mm, "end": v(9.9, -78.75) * mm});
            skPoint(sketch, "E10.39.1", {"position": v(8.13, -98.09) * mm});
            skPoint(sketch, "E10.39.2", {"position": v(8, -96.5) * mm});
            skPoint(sketch, "E10.39.3", {"position": v(10.04, -80.34) * mm});
            skLineSegment(sketch, "E10.39.4", {"start": v(8.13, -98.09) * mm, "end": v(10.04, -80.34) * mm});
            skPoint(sketch, "E10.39.5", {"position": v(3.32, -80.9) * mm});
            skLineSegment(sketch, "E10.39.6", {"start": v(8, -96.5) * mm, "end": v(3.19, -79.31) * mm});
            skLineSegment(sketch, "E10.39.7", {"start": v(3.32, -80.9) * mm, "end": v(8.13, -98.09) * mm});
            skLineSegment(sketch, "E10.40.0", {"start": v(15.94, -95.52) * mm, "end": v(16.38, -77.67) * mm});
            skPoint(sketch, "E10.40.1", {"position": v(16.2, -97.08) * mm});
            skPoint(sketch, "E10.40.2", {"position": v(15.94, -95.52) * mm});
            skPoint(sketch, "E10.40.3", {"position": v(16.64, -79.23) * mm});
            skLineSegment(sketch, "E10.40.4", {"start": v(16.2, -97.08) * mm, "end": v(16.64, -79.23) * mm});
            skPoint(sketch, "E10.40.5", {"position": v(9.99, -80.34) * mm});
            skLineSegment(sketch, "E10.40.6", {"start": v(15.94, -95.52) * mm, "end": v(9.73, -78.78) * mm});
            skLineSegment(sketch, "E10.40.7", {"start": v(9.99, -80.34) * mm, "end": v(16.2, -97.08) * mm});
            skLineSegment(sketch, "E10.41.0", {"start": v(23.77, -93.87) * mm, "end": v(22.74, -76.05) * mm});
            skPoint(sketch, "E10.41.1", {"position": v(24.16, -95.41) * mm});
            skPoint(sketch, "E10.41.2", {"position": v(23.77, -93.87) * mm});
            skPoint(sketch, "E10.41.3", {"position": v(23.13, -77.59) * mm});
            skLineSegment(sketch, "E10.41.4", {"start": v(24.16, -95.41) * mm, "end": v(23.13, -77.59) * mm});
            skPoint(sketch, "E10.41.5", {"position": v(16.59, -79.24) * mm});
            skLineSegment(sketch, "E10.41.6", {"start": v(23.77, -93.87) * mm, "end": v(16.2, -77.7) * mm});
            skLineSegment(sketch, "E10.41.7", {"start": v(16.59, -79.24) * mm, "end": v(24.16, -95.41) * mm});
            skLineSegment(sketch, "E10.42.0", {"start": v(31.44, -91.6) * mm, "end": v(28.94, -73.91) * mm});
            skPoint(sketch, "E10.42.1", {"position": v(31.96, -93.1) * mm});
            skPoint(sketch, "E10.42.2", {"position": v(31.44, -91.6) * mm});
            skPoint(sketch, "E10.42.3", {"position": v(29.45, -75.41) * mm});
            skLineSegment(sketch, "E10.42.4", {"start": v(31.96, -93.1) * mm, "end": v(29.45, -75.41) * mm});
            skPoint(sketch, "E10.42.5", {"position": v(23.08, -77.6) * mm});
            skLineSegment(sketch, "E10.42.6", {"start": v(31.44, -91.6) * mm, "end": v(22.56, -76.1) * mm});
            skLineSegment(sketch, "E10.42.7", {"start": v(23.08, -77.6) * mm, "end": v(31.96, -93.1) * mm});
            skLineSegment(sketch, "E10.43.0", {"start": v(38.9, -88.68) * mm, "end": v(34.94, -71.27) * mm});
            skPoint(sketch, "E10.43.1", {"position": v(39.54, -90.13) * mm});
            skPoint(sketch, "E10.43.2", {"position": v(38.9, -88.68) * mm});
            skPoint(sketch, "E10.43.3", {"position": v(35.58, -72.72) * mm});
            skLineSegment(sketch, "E10.43.4", {"start": v(39.54, -90.13) * mm, "end": v(35.58, -72.72) * mm});
            skPoint(sketch, "E10.43.5", {"position": v(29.4, -75.43) * mm});
            skLineSegment(sketch, "E10.43.6", {"start": v(38.9, -88.68) * mm, "end": v(28.77, -73.98) * mm});
            skLineSegment(sketch, "E10.43.7", {"start": v(29.4, -75.43) * mm, "end": v(39.54, -90.13) * mm});
            skLineSegment(sketch, "E10.44.0", {"start": v(46.09, -85.17) * mm, "end": v(40.7, -68.14) * mm});
            skPoint(sketch, "E10.44.1", {"position": v(46.85, -86.56) * mm});
            skPoint(sketch, "E10.44.2", {"position": v(46.09, -85.17) * mm});
            skPoint(sketch, "E10.44.3", {"position": v(41.47, -69.54) * mm});
            skLineSegment(sketch, "E10.44.4", {"start": v(46.85, -86.56) * mm, "end": v(41.47, -69.54) * mm});
            skPoint(sketch, "E10.44.5", {"position": v(35.53, -72.75) * mm});
            skLineSegment(sketch, "E10.44.6", {"start": v(46.09, -85.17) * mm, "end": v(34.78, -71.35) * mm});
            skLineSegment(sketch, "E10.44.7", {"start": v(35.53, -72.75) * mm, "end": v(46.85, -86.56) * mm});
            skLineSegment(sketch, "E10.45.0", {"start": v(52.97, -81.07) * mm, "end": v(46.2, -64.55) * mm});
            skPoint(sketch, "E10.45.1", {"position": v(53.83, -82.4) * mm});
            skPoint(sketch, "E10.45.2", {"position": v(52.97, -81.07) * mm});
            skPoint(sketch, "E10.45.3", {"position": v(47.07, -65.87) * mm});
            skLineSegment(sketch, "E10.45.4", {"start": v(53.83, -82.4) * mm, "end": v(47.07, -65.87) * mm});
            skPoint(sketch, "E10.45.5", {"position": v(41.42, -69.56) * mm});
            skLineSegment(sketch, "E10.45.6", {"start": v(52.97, -81.07) * mm, "end": v(40.55, -68.23) * mm});
            skLineSegment(sketch, "E10.45.7", {"start": v(41.42, -69.56) * mm, "end": v(53.83, -82.4) * mm});
            skLineSegment(sketch, "E10.46.0", {"start": v(59.48, -76.42) * mm, "end": v(51.37, -60.51) * mm});
            skPoint(sketch, "E10.46.1", {"position": v(60.45, -77.67) * mm});
            skPoint(sketch, "E10.46.2", {"position": v(59.48, -76.42) * mm});
            skPoint(sketch, "E10.46.3", {"position": v(52.34, -61.76) * mm});
            skLineSegment(sketch, "E10.46.4", {"start": v(60.45, -77.67) * mm, "end": v(52.34, -61.76) * mm});
            skPoint(sketch, "E10.46.5", {"position": v(47.02, -65.9) * mm});
            skLineSegment(sketch, "E10.46.6", {"start": v(59.48, -76.42) * mm, "end": v(46.05, -64.65) * mm});
            skLineSegment(sketch, "E10.46.7", {"start": v(47.02, -65.9) * mm, "end": v(60.45, -77.67) * mm});
            skLineSegment(sketch, "E10.47.0", {"start": v(65.59, -71.25) * mm, "end": v(56.2, -56.06) * mm});
            skPoint(sketch, "E10.47.1", {"position": v(66.66, -72.41) * mm});
            skPoint(sketch, "E10.47.2", {"position": v(65.59, -71.25) * mm});
            skPoint(sketch, "E10.47.3", {"position": v(57.27, -57.23) * mm});
            skLineSegment(sketch, "E10.47.4", {"start": v(66.66, -72.41) * mm, "end": v(57.27, -57.23) * mm});
            skPoint(sketch, "E10.47.5", {"position": v(52.3, -61.8) * mm});
            skLineSegment(sketch, "E10.47.6", {"start": v(65.59, -71.25) * mm, "end": v(51.23, -60.63) * mm});
            skLineSegment(sketch, "E10.47.7", {"start": v(52.3, -61.8) * mm, "end": v(66.66, -72.41) * mm});
            skLineSegment(sketch, "E10.48.0", {"start": v(71.25, -65.59) * mm, "end": v(60.63, -51.23) * mm});
            skPoint(sketch, "E10.48.1", {"position": v(72.41, -66.66) * mm});
            skPoint(sketch, "E10.48.2", {"position": v(71.25, -65.59) * mm});
            skPoint(sketch, "E10.48.3", {"position": v(61.8, -52.3) * mm});
            skLineSegment(sketch, "E10.48.4", {"start": v(72.41, -66.66) * mm, "end": v(61.8, -52.3) * mm});
            skPoint(sketch, "E10.48.5", {"position": v(57.23, -57.27) * mm});
            skLineSegment(sketch, "E10.48.6", {"start": v(71.25, -65.59) * mm, "end": v(56.06, -56.2) * mm});
            skLineSegment(sketch, "E10.48.7", {"start": v(57.23, -57.27) * mm, "end": v(72.41, -66.66) * mm});
            skLineSegment(sketch, "E10.49.0", {"start": v(76.42, -59.48) * mm, "end": v(64.65, -46.05) * mm});
            skPoint(sketch, "E10.49.1", {"position": v(77.67, -60.45) * mm});
            skPoint(sketch, "E10.49.2", {"position": v(76.42, -59.48) * mm});
            skPoint(sketch, "E10.49.3", {"position": v(65.9, -47.02) * mm});
            skLineSegment(sketch, "E10.49.4", {"start": v(77.67, -60.45) * mm, "end": v(65.9, -47.02) * mm});
            skPoint(sketch, "E10.49.5", {"position": v(61.76, -52.34) * mm});
            skLineSegment(sketch, "E10.49.6", {"start": v(76.42, -59.48) * mm, "end": v(60.51, -51.37) * mm});
            skLineSegment(sketch, "E10.49.7", {"start": v(61.76, -52.34) * mm, "end": v(77.67, -60.45) * mm});
            skLineSegment(sketch, "E10.50.0", {"start": v(81.07, -52.97) * mm, "end": v(68.23, -40.55) * mm});
            skPoint(sketch, "E10.50.1", {"position": v(82.4, -53.83) * mm});
            skPoint(sketch, "E10.50.2", {"position": v(81.07, -52.97) * mm});
            skPoint(sketch, "E10.50.3", {"position": v(69.56, -41.42) * mm});
            skLineSegment(sketch, "E10.50.4", {"start": v(82.4, -53.83) * mm, "end": v(69.56, -41.42) * mm});
            skPoint(sketch, "E10.50.5", {"position": v(65.87, -47.07) * mm});
            skLineSegment(sketch, "E10.50.6", {"start": v(81.07, -52.97) * mm, "end": v(64.55, -46.2) * mm});
            skLineSegment(sketch, "E10.50.7", {"start": v(65.87, -47.07) * mm, "end": v(82.4, -53.83) * mm});
            skLineSegment(sketch, "E10.51.0", {"start": v(85.17, -46.09) * mm, "end": v(71.35, -34.78) * mm});
            skPoint(sketch, "E10.51.1", {"position": v(86.56, -46.85) * mm});
            skPoint(sketch, "E10.51.2", {"position": v(85.17, -46.09) * mm});
            skPoint(sketch, "E10.51.3", {"position": v(72.75, -35.53) * mm});
            skLineSegment(sketch, "E10.51.4", {"start": v(86.56, -46.85) * mm, "end": v(72.75, -35.53) * mm});
            skPoint(sketch, "E10.51.5", {"position": v(69.54, -41.47) * mm});
            skLineSegment(sketch, "E10.51.6", {"start": v(85.17, -46.09) * mm, "end": v(68.14, -40.7) * mm});
            skLineSegment(sketch, "E10.51.7", {"start": v(69.54, -41.47) * mm, "end": v(86.56, -46.85) * mm});
            skLineSegment(sketch, "E10.52.0", {"start": v(88.68, -38.9) * mm, "end": v(73.98, -28.77) * mm});
            skPoint(sketch, "E10.52.1", {"position": v(90.13, -39.54) * mm});
            skPoint(sketch, "E10.52.2", {"position": v(88.68, -38.9) * mm});
            skPoint(sketch, "E10.52.3", {"position": v(75.43, -29.4) * mm});
            skLineSegment(sketch, "E10.52.4", {"start": v(90.13, -39.54) * mm, "end": v(75.43, -29.4) * mm});
            skPoint(sketch, "E10.52.5", {"position": v(72.72, -35.58) * mm});
            skLineSegment(sketch, "E10.52.6", {"start": v(88.68, -38.9) * mm, "end": v(71.27, -34.94) * mm});
            skLineSegment(sketch, "E10.52.7", {"start": v(72.72, -35.58) * mm, "end": v(90.13, -39.54) * mm});
            skLineSegment(sketch, "E10.53.0", {"start": v(91.6, -31.44) * mm, "end": v(76.1, -22.56) * mm});
            skPoint(sketch, "E10.53.1", {"position": v(93.1, -31.96) * mm});
            skPoint(sketch, "E10.53.2", {"position": v(91.6, -31.44) * mm});
            skPoint(sketch, "E10.53.3", {"position": v(77.6, -23.08) * mm});
            skLineSegment(sketch, "E10.53.4", {"start": v(93.1, -31.96) * mm, "end": v(77.6, -23.08) * mm});
            skPoint(sketch, "E10.53.5", {"position": v(75.41, -29.45) * mm});
            skLineSegment(sketch, "E10.53.6", {"start": v(91.6, -31.44) * mm, "end": v(73.91, -28.94) * mm});
            skLineSegment(sketch, "E10.53.7", {"start": v(75.41, -29.45) * mm, "end": v(93.1, -31.96) * mm});
            skLineSegment(sketch, "E10.54.0", {"start": v(93.87, -23.77) * mm, "end": v(77.7, -16.2) * mm});
            skPoint(sketch, "E10.54.1", {"position": v(95.41, -24.16) * mm});
            skPoint(sketch, "E10.54.2", {"position": v(93.87, -23.77) * mm});
            skPoint(sketch, "E10.54.3", {"position": v(79.24, -16.59) * mm});
            skLineSegment(sketch, "E10.54.4", {"start": v(95.41, -24.16) * mm, "end": v(79.24, -16.59) * mm});
            skPoint(sketch, "E10.54.5", {"position": v(77.59, -23.13) * mm});
            skLineSegment(sketch, "E10.54.6", {"start": v(93.87, -23.77) * mm, "end": v(76.05, -22.74) * mm});
            skLineSegment(sketch, "E10.54.7", {"start": v(77.59, -23.13) * mm, "end": v(95.41, -24.16) * mm});
            skLineSegment(sketch, "E10.55.0", {"start": v(95.52, -15.94) * mm, "end": v(78.78, -9.73) * mm});
            skPoint(sketch, "E10.55.1", {"position": v(97.08, -16.2) * mm});
            skPoint(sketch, "E10.55.2", {"position": v(95.52, -15.94) * mm});
            skPoint(sketch, "E10.55.3", {"position": v(80.34, -9.99) * mm});
            skLineSegment(sketch, "E10.55.4", {"start": v(97.08, -16.2) * mm, "end": v(80.34, -9.99) * mm});
            skPoint(sketch, "E10.55.5", {"position": v(79.23, -16.64) * mm});
            skLineSegment(sketch, "E10.55.6", {"start": v(95.52, -15.94) * mm, "end": v(77.67, -16.38) * mm});
            skLineSegment(sketch, "E10.55.7", {"start": v(79.23, -16.64) * mm, "end": v(97.08, -16.2) * mm});
            skLineSegment(sketch, "E10.56.0", {"start": v(96.5, -8) * mm, "end": v(79.31, -3.19) * mm});
            skPoint(sketch, "E10.56.1", {"position": v(98.09, -8.13) * mm});
            skPoint(sketch, "E10.56.2", {"position": v(96.5, -8) * mm});
            skPoint(sketch, "E10.56.3", {"position": v(80.9, -3.32) * mm});
            skLineSegment(sketch, "E10.56.4", {"start": v(98.09, -8.13) * mm, "end": v(80.9, -3.32) * mm});
            skPoint(sketch, "E10.56.5", {"position": v(80.34, -10.04) * mm});
            skLineSegment(sketch, "E10.56.6", {"start": v(96.5, -8) * mm, "end": v(78.75, -9.9) * mm});
            skLineSegment(sketch, "E10.56.7", {"start": v(80.34, -10.04) * mm, "end": v(98.09, -8.13) * mm});
            skLineSegment(sketch, "E10.57.0", {"start": v(96.84, 0) * mm, "end": v(79.3, 3.37) * mm});
            skPoint(sketch, "E10.57.1", {"position": v(98.43, 0) * mm});
            skPoint(sketch, "E10.57.2", {"position": v(96.84, 0) * mm});
            skPoint(sketch, "E10.57.3", {"position": v(80.9, 3.37) * mm});
            skLineSegment(sketch, "E10.57.4", {"start": v(98.43, 0) * mm, "end": v(80.9, 3.37) * mm});
            skPoint(sketch, "E10.57.5", {"position": v(80.9, -3.37) * mm});
            skLineSegment(sketch, "E10.57.6", {"start": v(96.84, 0) * mm, "end": v(79.3, -3.37) * mm});
            skLineSegment(sketch, "E10.57.7", {"start": v(80.9, -3.37) * mm, "end": v(98.43, 0) * mm});
            skLineSegment(sketch, "E10.58.0", {"start": v(96.5, 8) * mm, "end": v(78.75, 9.9) * mm});
            skPoint(sketch, "E10.58.1", {"position": v(98.09, 8.13) * mm});
            skPoint(sketch, "E10.58.2", {"position": v(96.5, 8) * mm});
            skPoint(sketch, "E10.58.3", {"position": v(80.34, 10.04) * mm});
            skLineSegment(sketch, "E10.58.4", {"start": v(98.09, 8.13) * mm, "end": v(80.34, 10.04) * mm});
            skPoint(sketch, "E10.58.5", {"position": v(80.9, 3.32) * mm});
            skLineSegment(sketch, "E10.58.6", {"start": v(96.5, 8) * mm, "end": v(79.31, 3.19) * mm});
            skLineSegment(sketch, "E10.58.7", {"start": v(80.9, 3.32) * mm, "end": v(98.09, 8.13) * mm});
            skLineSegment(sketch, "E10.59.0", {"start": v(95.52, 15.94) * mm, "end": v(77.67, 16.38) * mm});
            skPoint(sketch, "E10.59.1", {"position": v(97.08, 16.2) * mm});
            skPoint(sketch, "E10.59.2", {"position": v(95.52, 15.94) * mm});
            skPoint(sketch, "E10.59.3", {"position": v(79.23, 16.64) * mm});
            skLineSegment(sketch, "E10.59.4", {"start": v(97.08, 16.2) * mm, "end": v(79.23, 16.64) * mm});
            skPoint(sketch, "E10.59.5", {"position": v(80.34, 9.99) * mm});
            skLineSegment(sketch, "E10.59.6", {"start": v(95.52, 15.94) * mm, "end": v(78.78, 9.73) * mm});
            skLineSegment(sketch, "E10.59.7", {"start": v(80.34, 9.99) * mm, "end": v(97.08, 16.2) * mm});
            skLineSegment(sketch, "E10.60.0", {"start": v(93.87, 23.77) * mm, "end": v(76.05, 22.74) * mm});
            skPoint(sketch, "E10.60.1", {"position": v(95.41, 24.16) * mm});
            skPoint(sketch, "E10.60.2", {"position": v(93.87, 23.77) * mm});
            skPoint(sketch, "E10.60.3", {"position": v(77.59, 23.13) * mm});
            skLineSegment(sketch, "E10.60.4", {"start": v(95.41, 24.16) * mm, "end": v(77.59, 23.13) * mm});
            skPoint(sketch, "E10.60.5", {"position": v(79.24, 16.59) * mm});
            skLineSegment(sketch, "E10.60.6", {"start": v(93.87, 23.77) * mm, "end": v(77.7, 16.2) * mm});
            skLineSegment(sketch, "E10.60.7", {"start": v(79.24, 16.59) * mm, "end": v(95.41, 24.16) * mm});
            skLineSegment(sketch, "E10.61.0", {"start": v(91.6, 31.44) * mm, "end": v(73.91, 28.94) * mm});
            skPoint(sketch, "E10.61.1", {"position": v(93.1, 31.96) * mm});
            skPoint(sketch, "E10.61.2", {"position": v(91.6, 31.44) * mm});
            skPoint(sketch, "E10.61.3", {"position": v(75.41, 29.45) * mm});
            skLineSegment(sketch, "E10.61.4", {"start": v(93.1, 31.96) * mm, "end": v(75.41, 29.45) * mm});
            skPoint(sketch, "E10.61.5", {"position": v(77.6, 23.08) * mm});
            skLineSegment(sketch, "E10.61.6", {"start": v(91.6, 31.44) * mm, "end": v(76.1, 22.56) * mm});
            skLineSegment(sketch, "E10.61.7", {"start": v(77.6, 23.08) * mm, "end": v(93.1, 31.96) * mm});
            skLineSegment(sketch, "E10.62.0", {"start": v(88.68, 38.9) * mm, "end": v(71.27, 34.94) * mm});
            skPoint(sketch, "E10.62.1", {"position": v(90.13, 39.54) * mm});
            skPoint(sketch, "E10.62.2", {"position": v(88.68, 38.9) * mm});
            skPoint(sketch, "E10.62.3", {"position": v(72.72, 35.58) * mm});
            skLineSegment(sketch, "E10.62.4", {"start": v(90.13, 39.54) * mm, "end": v(72.72, 35.58) * mm});
            skPoint(sketch, "E10.62.5", {"position": v(75.43, 29.4) * mm});
            skLineSegment(sketch, "E10.62.6", {"start": v(88.68, 38.9) * mm, "end": v(73.98, 28.77) * mm});
            skLineSegment(sketch, "E10.62.7", {"start": v(75.43, 29.4) * mm, "end": v(90.13, 39.54) * mm});
            skLineSegment(sketch, "E10.63.0", {"start": v(85.17, 46.09) * mm, "end": v(68.14, 40.7) * mm});
            skPoint(sketch, "E10.63.1", {"position": v(86.56, 46.85) * mm});
            skPoint(sketch, "E10.63.2", {"position": v(85.17, 46.09) * mm});
            skPoint(sketch, "E10.63.3", {"position": v(69.54, 41.47) * mm});
            skLineSegment(sketch, "E10.63.4", {"start": v(86.56, 46.85) * mm, "end": v(69.54, 41.47) * mm});
            skPoint(sketch, "E10.63.5", {"position": v(72.75, 35.53) * mm});
            skLineSegment(sketch, "E10.63.6", {"start": v(85.17, 46.09) * mm, "end": v(71.35, 34.78) * mm});
            skLineSegment(sketch, "E10.63.7", {"start": v(72.75, 35.53) * mm, "end": v(86.56, 46.85) * mm});
            skLineSegment(sketch, "E10.64.0", {"start": v(81.07, 52.97) * mm, "end": v(64.55, 46.2) * mm});
            skPoint(sketch, "E10.64.1", {"position": v(82.4, 53.83) * mm});
            skPoint(sketch, "E10.64.2", {"position": v(81.07, 52.97) * mm});
            skPoint(sketch, "E10.64.3", {"position": v(65.87, 47.07) * mm});
            skLineSegment(sketch, "E10.64.4", {"start": v(82.4, 53.83) * mm, "end": v(65.87, 47.07) * mm});
            skPoint(sketch, "E10.64.5", {"position": v(69.56, 41.42) * mm});
            skLineSegment(sketch, "E10.64.6", {"start": v(81.07, 52.97) * mm, "end": v(68.23, 40.55) * mm});
            skLineSegment(sketch, "E10.64.7", {"start": v(69.56, 41.42) * mm, "end": v(82.4, 53.83) * mm});
            skLineSegment(sketch, "E10.65.0", {"start": v(76.42, 59.48) * mm, "end": v(60.51, 51.37) * mm});
            skPoint(sketch, "E10.65.1", {"position": v(77.67, 60.45) * mm});
            skPoint(sketch, "E10.65.2", {"position": v(76.42, 59.48) * mm});
            skPoint(sketch, "E10.65.3", {"position": v(61.76, 52.34) * mm});
            skLineSegment(sketch, "E10.65.4", {"start": v(77.67, 60.45) * mm, "end": v(61.76, 52.34) * mm});
            skPoint(sketch, "E10.65.5", {"position": v(65.9, 47.02) * mm});
            skLineSegment(sketch, "E10.65.6", {"start": v(76.42, 59.48) * mm, "end": v(64.65, 46.05) * mm});
            skLineSegment(sketch, "E10.65.7", {"start": v(65.9, 47.02) * mm, "end": v(77.67, 60.45) * mm});
            skLineSegment(sketch, "E10.66.0", {"start": v(71.25, 65.59) * mm, "end": v(56.06, 56.2) * mm});
            skPoint(sketch, "E10.66.1", {"position": v(72.41, 66.66) * mm});
            skPoint(sketch, "E10.66.2", {"position": v(71.25, 65.59) * mm});
            skPoint(sketch, "E10.66.3", {"position": v(57.23, 57.27) * mm});
            skLineSegment(sketch, "E10.66.4", {"start": v(72.41, 66.66) * mm, "end": v(57.23, 57.27) * mm});
            skPoint(sketch, "E10.66.5", {"position": v(61.8, 52.3) * mm});
            skLineSegment(sketch, "E10.66.6", {"start": v(71.25, 65.59) * mm, "end": v(60.63, 51.23) * mm});
            skLineSegment(sketch, "E10.66.7", {"start": v(61.8, 52.3) * mm, "end": v(72.41, 66.66) * mm});
            skLineSegment(sketch, "E10.67.0", {"start": v(65.59, 71.25) * mm, "end": v(51.23, 60.63) * mm});
            skPoint(sketch, "E10.67.1", {"position": v(66.66, 72.41) * mm});
            skPoint(sketch, "E10.67.2", {"position": v(65.59, 71.25) * mm});
            skPoint(sketch, "E10.67.3", {"position": v(52.3, 61.8) * mm});
            skLineSegment(sketch, "E10.67.4", {"start": v(66.66, 72.41) * mm, "end": v(52.3, 61.8) * mm});
            skPoint(sketch, "E10.67.5", {"position": v(57.27, 57.23) * mm});
            skLineSegment(sketch, "E10.67.6", {"start": v(65.59, 71.25) * mm, "end": v(56.2, 56.06) * mm});
            skLineSegment(sketch, "E10.67.7", {"start": v(57.27, 57.23) * mm, "end": v(66.66, 72.41) * mm});
            skLineSegment(sketch, "E10.68.0", {"start": v(59.48, 76.42) * mm, "end": v(46.05, 64.65) * mm});
            skPoint(sketch, "E10.68.1", {"position": v(60.45, 77.67) * mm});
            skPoint(sketch, "E10.68.2", {"position": v(59.48, 76.42) * mm});
            skPoint(sketch, "E10.68.3", {"position": v(47.02, 65.9) * mm});
            skLineSegment(sketch, "E10.68.4", {"start": v(60.45, 77.67) * mm, "end": v(47.02, 65.9) * mm});
            skPoint(sketch, "E10.68.5", {"position": v(52.34, 61.76) * mm});
            skLineSegment(sketch, "E10.68.6", {"start": v(59.48, 76.42) * mm, "end": v(51.37, 60.51) * mm});
            skLineSegment(sketch, "E10.68.7", {"start": v(52.34, 61.76) * mm, "end": v(60.45, 77.67) * mm});
            skLineSegment(sketch, "E10.69.0", {"start": v(52.97, 81.07) * mm, "end": v(40.55, 68.23) * mm});
            skPoint(sketch, "E10.69.1", {"position": v(53.83, 82.4) * mm});
            skPoint(sketch, "E10.69.2", {"position": v(52.97, 81.07) * mm});
            skPoint(sketch, "E10.69.3", {"position": v(41.42, 69.56) * mm});
            skLineSegment(sketch, "E10.69.4", {"start": v(53.83, 82.4) * mm, "end": v(41.42, 69.56) * mm});
            skPoint(sketch, "E10.69.5", {"position": v(47.07, 65.87) * mm});
            skLineSegment(sketch, "E10.69.6", {"start": v(52.97, 81.07) * mm, "end": v(46.2, 64.55) * mm});
            skLineSegment(sketch, "E10.69.7", {"start": v(47.07, 65.87) * mm, "end": v(53.83, 82.4) * mm});
            skLineSegment(sketch, "E10.70.0", {"start": v(46.09, 85.17) * mm, "end": v(34.78, 71.35) * mm});
            skPoint(sketch, "E10.70.1", {"position": v(46.85, 86.56) * mm});
            skPoint(sketch, "E10.70.2", {"position": v(46.09, 85.17) * mm});
            skPoint(sketch, "E10.70.3", {"position": v(35.53, 72.75) * mm});
            skLineSegment(sketch, "E10.70.4", {"start": v(46.85, 86.56) * mm, "end": v(35.53, 72.75) * mm});
            skPoint(sketch, "E10.70.5", {"position": v(41.47, 69.54) * mm});
            skLineSegment(sketch, "E10.70.6", {"start": v(46.09, 85.17) * mm, "end": v(40.7, 68.14) * mm});
            skLineSegment(sketch, "E10.70.7", {"start": v(41.47, 69.54) * mm, "end": v(46.85, 86.56) * mm});
            skLineSegment(sketch, "E10.71.0", {"start": v(38.9, 88.68) * mm, "end": v(28.77, 73.98) * mm});
            skPoint(sketch, "E10.71.1", {"position": v(39.54, 90.13) * mm});
            skPoint(sketch, "E10.71.2", {"position": v(38.9, 88.68) * mm});
            skPoint(sketch, "E10.71.3", {"position": v(29.4, 75.43) * mm});
            skLineSegment(sketch, "E10.71.4", {"start": v(39.54, 90.13) * mm, "end": v(29.4, 75.43) * mm});
            skPoint(sketch, "E10.71.5", {"position": v(35.58, 72.72) * mm});
            skLineSegment(sketch, "E10.71.6", {"start": v(38.9, 88.68) * mm, "end": v(34.94, 71.27) * mm});
            skLineSegment(sketch, "E10.71.7", {"start": v(35.58, 72.72) * mm, "end": v(39.54, 90.13) * mm});
            skLineSegment(sketch, "E10.72.0", {"start": v(31.44, 91.6) * mm, "end": v(22.56, 76.1) * mm});
            skPoint(sketch, "E10.72.1", {"position": v(31.96, 93.1) * mm});
            skPoint(sketch, "E10.72.2", {"position": v(31.44, 91.6) * mm});
            skPoint(sketch, "E10.72.3", {"position": v(23.08, 77.6) * mm});
            skLineSegment(sketch, "E10.72.4", {"start": v(31.96, 93.1) * mm, "end": v(23.08, 77.6) * mm});
            skPoint(sketch, "E10.72.5", {"position": v(29.45, 75.41) * mm});
            skLineSegment(sketch, "E10.72.6", {"start": v(31.44, 91.6) * mm, "end": v(28.94, 73.91) * mm});
            skLineSegment(sketch, "E10.72.7", {"start": v(29.45, 75.41) * mm, "end": v(31.96, 93.1) * mm});
            skLineSegment(sketch, "E10.73.0", {"start": v(23.77, 93.87) * mm, "end": v(16.2, 77.7) * mm});
            skPoint(sketch, "E10.73.1", {"position": v(24.16, 95.41) * mm});
            skPoint(sketch, "E10.73.2", {"position": v(23.77, 93.87) * mm});
            skPoint(sketch, "E10.73.3", {"position": v(16.59, 79.24) * mm});
            skLineSegment(sketch, "E10.73.4", {"start": v(24.16, 95.41) * mm, "end": v(16.59, 79.24) * mm});
            skPoint(sketch, "E10.73.5", {"position": v(23.13, 77.59) * mm});
            skLineSegment(sketch, "E10.73.6", {"start": v(23.77, 93.87) * mm, "end": v(22.74, 76.05) * mm});
            skLineSegment(sketch, "E10.73.7", {"start": v(23.13, 77.59) * mm, "end": v(24.16, 95.41) * mm});
            skLineSegment(sketch, "E10.74.0", {"start": v(15.94, 95.52) * mm, "end": v(9.73, 78.78) * mm});
            skPoint(sketch, "E10.74.1", {"position": v(16.2, 97.08) * mm});
            skPoint(sketch, "E10.74.2", {"position": v(15.94, 95.52) * mm});
            skPoint(sketch, "E10.74.3", {"position": v(9.99, 80.34) * mm});
            skLineSegment(sketch, "E10.74.4", {"start": v(16.2, 97.08) * mm, "end": v(9.99, 80.34) * mm});
            skPoint(sketch, "E10.74.5", {"position": v(16.64, 79.23) * mm});
            skLineSegment(sketch, "E10.74.6", {"start": v(15.94, 95.52) * mm, "end": v(16.38, 77.67) * mm});
            skLineSegment(sketch, "E10.74.7", {"start": v(16.64, 79.23) * mm, "end": v(16.2, 97.08) * mm});
            skLineSegment(sketch, "E11.2.75.0", {"start": v(8, 96.5) * mm, "end": v(3.19, 79.31) * mm});
            skPoint(sketch, "E11.3.75.0", {"position": v(8.13, 98.09) * mm});
            skPoint(sketch, "E11.4.75.0", {"position": v(8, 96.5) * mm});
            skPoint(sketch, "E11.5.75.0", {"position": v(3.32, 80.9) * mm});
            skLineSegment(sketch, "E11.6.75.0", {"start": v(8.13, 98.09) * mm, "end": v(3.32, 80.9) * mm});
            skPoint(sketch, "E11.9.75.0", {"position": v(10.04, 80.34) * mm});
            skLineSegment(sketch, "E11.10.75.0", {"start": v(8, 96.5) * mm, "end": v(9.9, 78.75) * mm});
            skLineSegment(sketch, "E11.13.75.0", {"start": v(10.04, 80.34) * mm, "end": v(8.13, 98.09) * mm});
            skCircle(sketch, "E12", {"center": v(0, 0) * mm, "radius": 3.18 * mm});
            skSolve(sketch);
        }
        {
            var Q0;
            {var subQ333=sQuery(id+"F0.wireOp",EDGE,"E7");var subQ418=sQuery(id+"F0.wireOp",EDGE,"E6");var subQ419=makeQuery(id+"F0.imprint","INTERSECT",VERTEX,{"derivedFrom":[subQ418,subQ333]});Q0=makeQuery(id+"F0.imprint","IMPRINT",FACE,{"disambiguationData":[TD([[makeQuery(id+"F0.imprint","IMPRINT",EDGE,{"disambiguationData":[TD([[subQ419,-1.0]])],"derivedFrom":subQ418}),-1.0]])]});}
            var Q1;
            Q1=makeQuery(id+"F0.imprint","IMPRINT",FACE,{"disambiguationData":[TD([[makeQuery(id+"F0.imprint","IMPRINT",EDGE,{"derivedFrom":sQuery(id+"F0.wireOp",EDGE,"E12")}),1.0]])]});
            extrude(context, id + "F1", {"entities" : qUnion([Q0, Q1]), "oppositeDirection" : true, "depth" : 63.5 * mm});
        }
    });
